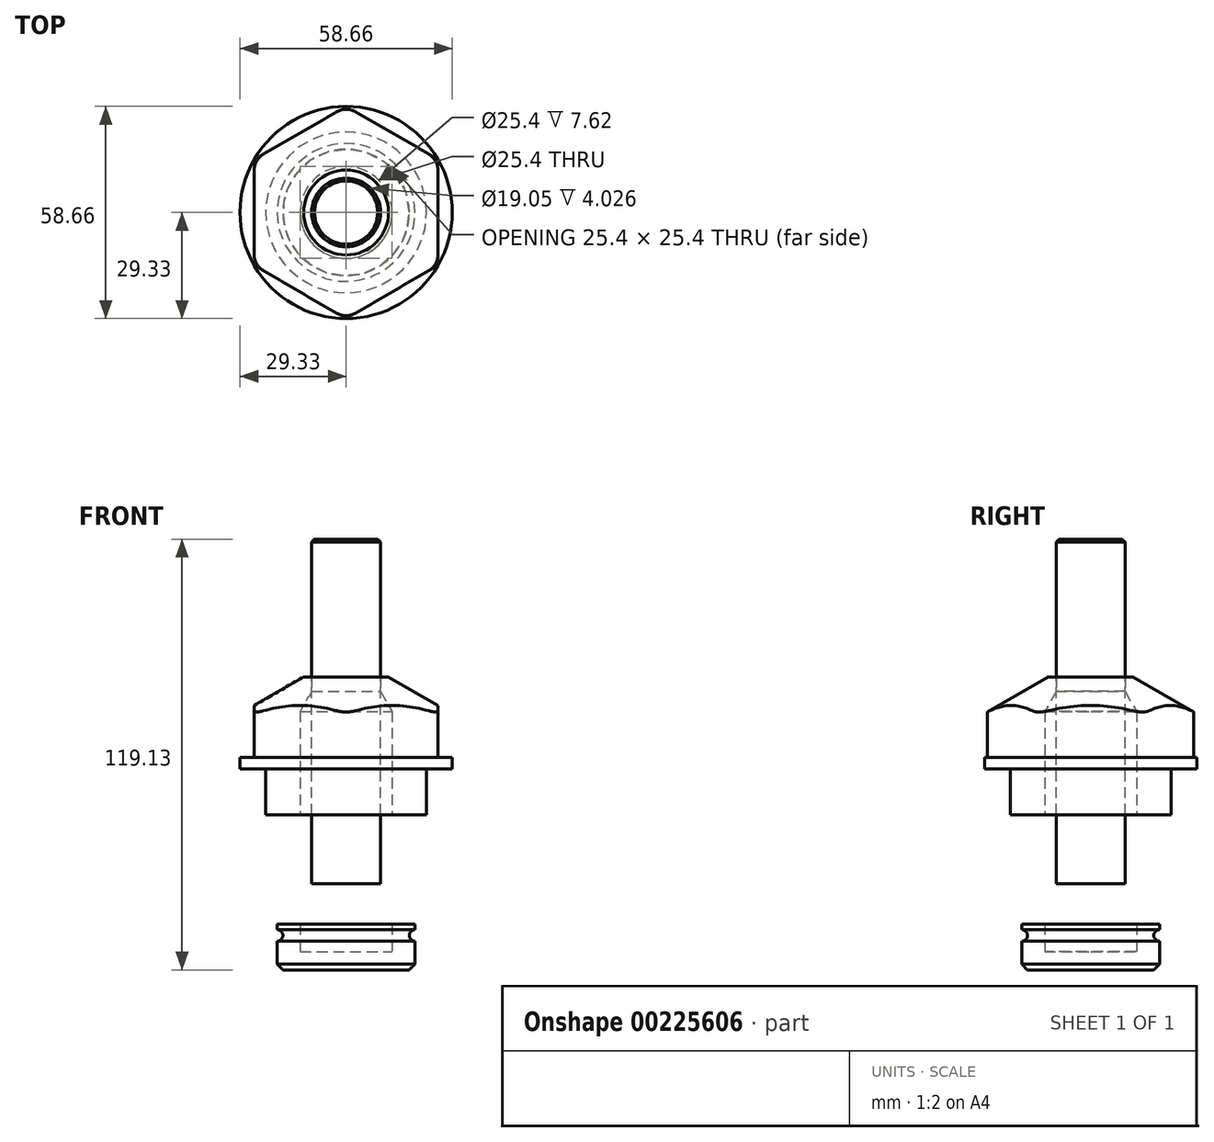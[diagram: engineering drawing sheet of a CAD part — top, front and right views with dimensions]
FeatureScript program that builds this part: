
annotation { "Feature Type Name" : "Feature", "Feature Type Description" : "" }
export const myFeature = defineFeature(function(context is Context, id is Id, definition is map)
    precondition{}
    {
        {
            var Q0;
            Q0=qCreatedBy(makeId("Top.planeOp"),FACE);
            var sketch = newSketch(context, id + "F0", { "sketchPlane" : qUnion([Q0])});
            skCircle(sketch, "E0", {"center": v(0, 0) * mm, "radius": 29.33 * mm});
            skLineSegment(sketch, "E1", {"start": v(0, 29.33) * mm, "end": v(0, -29.33) * mm, "construction": true});
            skLineSegment(sketch, "E2", {"start": v(-25.4, 14.66) * mm, "end": v(25.4, -14.66) * mm, "construction": true});
            skLineSegment(sketch, "E3", {"start": v(-25.4, -14.66) * mm, "end": v(25.4, 14.66) * mm, "construction": true});
            skLineSegment(sketch, "E4", {"start": v(-25.4, 14.66) * mm, "end": v(0, 29.33) * mm});
            skLineSegment(sketch, "E5", {"start": v(0, 29.33) * mm, "end": v(25.4, 14.66) * mm});
            skLineSegment(sketch, "E6", {"start": v(25.4, 14.66) * mm, "end": v(25.4, -14.66) * mm});
            skLineSegment(sketch, "E7", {"start": v(25.4, -14.66) * mm, "end": v(0, -29.33) * mm});
            skLineSegment(sketch, "E8", {"start": v(0, -29.33) * mm, "end": v(-25.4, -14.66) * mm});
            skLineSegment(sketch, "E9", {"start": v(-25.4, -14.66) * mm, "end": v(-25.4, 14.66) * mm});
            skCircle(sketch, "E10", {"center": v(0, 0) * mm, "radius": 7.94 * mm});
            skSolve(sketch);
        }
        {
            var Q0;
            Q0=makeQuery(id+"F0.imprint","IMPRINT",FACE,{"disambiguationData":[TD([[makeQuery(id+"F0.imprint","IMPRINT",EDGE,{"derivedFrom":sQuery(id+"F0.wireOp",EDGE,"E10")}),1.0]])]});
            var Q1;
            Q1=makeQuery(id+"F0.imprint","IMPRINT",FACE,{"disambiguationData":[TD([[makeQuery(id+"F0.imprint","IMPRINT",EDGE,{"derivedFrom":sQuery(id+"F0.wireOp",EDGE,"E4")}),-1.0]])]});
            extrude(context, id + "F1", {"entities" : qUnion([Q0, Q1]), "flatOperationType" : FlatOperationType.REMOVE, "depth" : 25.4 * mm, "offsetDistance" : 25.4 * mm, "domain" : OperationDomain.MODEL});
        }
        {
            var Q0;
            {var subQ0=sQuery(id+"F0.wireOp",EDGE,"E8");Q0=makeQuery(id+"F0.imprint","IMPRINT",FACE,{"disambiguationData":[TD([[makeQuery(id+"F0.imprint","IMPRINT",EDGE,{"derivedFrom":subQ0}),1.0]])]});}
            var Q1;
            {var subQ0=sQuery(id+"F0.wireOp",EDGE,"E7");Q1=makeQuery(id+"F0.imprint","IMPRINT",FACE,{"disambiguationData":[TD([[makeQuery(id+"F0.imprint","IMPRINT",EDGE,{"derivedFrom":subQ0}),1.0]])]});}
            var Q2;
            {var subQ0=sQuery(id+"F0.wireOp",EDGE,"E6");Q2=makeQuery(id+"F0.imprint","IMPRINT",FACE,{"disambiguationData":[TD([[makeQuery(id+"F0.imprint","IMPRINT",EDGE,{"derivedFrom":subQ0}),1.0]])]});}
            var Q3;
            Q3=makeQuery(id+"F0.imprint","IMPRINT",FACE,{"disambiguationData":[TD([[makeQuery(id+"F0.imprint","IMPRINT",EDGE,{"derivedFrom":sQuery(id+"F0.wireOp",EDGE,"E4")}),-1.0]])]});
            var Q4;
            {var subQ0=sQuery(id+"F0.wireOp",EDGE,"E5");Q4=makeQuery(id+"F0.imprint","IMPRINT",FACE,{"disambiguationData":[TD([[makeQuery(id+"F0.imprint","IMPRINT",EDGE,{"derivedFrom":subQ0}),1.0]])]});}
            var Q5;
            {var subQ0=sQuery(id+"F0.wireOp",EDGE,"E4");Q5=makeQuery(id+"F0.imprint","IMPRINT",FACE,{"disambiguationData":[TD([[makeQuery(id+"F0.imprint","IMPRINT",EDGE,{"derivedFrom":subQ0}),1.0]])]});}
            var Q6;
            {var subQ0=sQuery(id+"F0.wireOp",EDGE,"E9");Q6=makeQuery(id+"F0.imprint","IMPRINT",FACE,{"disambiguationData":[TD([[makeQuery(id+"F0.imprint","IMPRINT",EDGE,{"derivedFrom":subQ0}),1.0]])]});}
            extrude(context, id + "F2", {"entities" : qUnion([Q0, Q1, Q2, Q3, Q4, Q5, Q6]), "operationType" : NewBodyOperationType.ADD, "flatOperationType" : FlatOperationType.REMOVE, "depth" : 3.17 * mm, "offsetDistance" : 25.4 * mm, "domain" : OperationDomain.MODEL});
        }
        {
            var Q0;
            Q0=makeQuery(id+"F1.opExtrude","SWEPT_EDGE",EDGE,{"disambiguationData":[OSD([sQuery(id+"F0.wireOp",EDGE,"E0"),sQuery(id+"F0.wireOp",EDGE,"E7"),sQuery(id+"F0.wireOp",EDGE,"E8")])]});
            var Q1;
            Q1=makeQuery(id+"F1.opExtrude","SWEPT_EDGE",EDGE,{"disambiguationData":[OSD([sQuery(id+"F0.wireOp",EDGE,"E0"),sQuery(id+"F0.wireOp",EDGE,"E6"),sQuery(id+"F0.wireOp",EDGE,"E7")])]});
            var Q2;
            Q2=makeQuery(id+"F1.opExtrude","SWEPT_EDGE",EDGE,{"disambiguationData":[OSD([sQuery(id+"F0.wireOp",EDGE,"E0"),sQuery(id+"F0.wireOp",EDGE,"E5"),sQuery(id+"F0.wireOp",EDGE,"E6")])]});
            var Q3;
            Q3=makeQuery(id+"F1.opExtrude","SWEPT_EDGE",EDGE,{"disambiguationData":[OSD([sQuery(id+"F0.wireOp",EDGE,"E0"),sQuery(id+"F0.wireOp",EDGE,"E4"),sQuery(id+"F0.wireOp",EDGE,"E5")])]});
            var Q4;
            Q4=makeQuery(id+"F1.opExtrude","SWEPT_EDGE",EDGE,{"disambiguationData":[OSD([sQuery(id+"F0.wireOp",EDGE,"E0"),sQuery(id+"F0.wireOp",EDGE,"E4"),sQuery(id+"F0.wireOp",EDGE,"E9")])]});
            var Q5;
            Q5=makeQuery(id+"F1.opExtrude","SWEPT_EDGE",EDGE,{"disambiguationData":[OSD([sQuery(id+"F0.wireOp",EDGE,"E0"),sQuery(id+"F0.wireOp",EDGE,"E8"),sQuery(id+"F0.wireOp",EDGE,"E9")])]});
            fillet(context, id + "F3", {"entities" : qUnion([Q0, Q1, Q2, Q3, Q4, Q5]), "radius" : 5.08 * mm, "tangentPropagation" : true, "defaultsChanged" : false, "vertexSettings" : [], "allowEdgeOverflow" : false});
        }
        {
            var Q0;
            Q0=qCreatedBy(makeId("Right.planeOp"),FACE);
            var sketch = newSketch(context, id + "F4", { "sketchPlane" : qUnion([Q0])});
            skLineSegment(sketch, "E11", {"start": v(0, 52) * mm, "end": v(0, 0) * mm, "construction": true});
            skLineSegment(sketch, "E12", {"start": v(11.73, 25.4) * mm, "end": v(35.4, 11.74) * mm});
            skLineSegment(sketch, "E13", {"start": v(35.4, 11.74) * mm, "end": v(35.4, 25.4) * mm});
            skLineSegment(sketch, "E14", {"start": v(35.4, 25.4) * mm, "end": v(11.73, 25.4) * mm});
            skLineSegment(sketch, "E15.0", {"start": v(11.73, 25.4) * mm, "end": v(-11.73, 25.4) * mm});
            skLineSegment(sketch, "E16.bottom", {"start": v(0, 0) * mm, "end": v(22.23, 0) * mm});
            skLineSegment(sketch, "E16.top", {"start": v(0, -12.7) * mm, "end": v(22.23, -12.7) * mm});
            skLineSegment(sketch, "E16.left", {"start": v(0, 0) * mm, "end": v(0, -12.7) * mm});
            skLineSegment(sketch, "E16.right", {"start": v(22.23, 0) * mm, "end": v(22.23, -12.7) * mm});
            skLineSegment(sketch, "E17.bottom", {"start": v(0, -12.7) * mm, "end": v(19.05, -12.7) * mm});
            skLineSegment(sketch, "E17.top", {"start": v(0, -27.69) * mm, "end": v(19.05, -27.69) * mm});
            skLineSegment(sketch, "E17.left", {"start": v(0, -12.7) * mm, "end": v(0, -27.69) * mm});
            skLineSegment(sketch, "E17.right", {"start": v(19.05, -12.7) * mm, "end": v(19.05, -27.69) * mm});
            skLineSegment(sketch, "E18.bottom", {"start": v(17.78, -27.69) * mm, "end": v(0, -27.69) * mm});
            skLineSegment(sketch, "E18.top", {"start": v(17.78, -42.93) * mm, "end": v(0, -42.93) * mm});
            skLineSegment(sketch, "E18.left", {"start": v(17.78, -27.69) * mm, "end": v(17.78, -42.93) * mm});
            skLineSegment(sketch, "E18.right", {"start": v(0, -27.69) * mm, "end": v(0, -42.93) * mm});
            skLineSegment(sketch, "E19.bottom", {"start": v(0, -42.93) * mm, "end": v(19.05, -42.93) * mm});
            skLineSegment(sketch, "E19.top", {"start": v(0, -55.63) * mm, "end": v(19.05, -55.63) * mm});
            skLineSegment(sketch, "E19.left", {"start": v(0, -42.93) * mm, "end": v(0, -55.63) * mm});
            skLineSegment(sketch, "E19.right", {"start": v(19.05, -42.93) * mm, "end": v(19.05, -55.63) * mm});
            skCircle(sketch, "E20", {"center": v(19.05, -24.51) * mm, "radius": 1.59 * mm});
            skCircle(sketch, "E21", {"center": v(19.05, -46.1) * mm, "radius": 1.59 * mm});
            skCircle(sketch, "E22", {"center": v(0, -17.46) * mm, "radius": 3.18 * mm});
            skCircle(sketch, "E23", {"center": v(0, -35.3) * mm, "radius": 3.18 * mm});
            skSolve(sketch);
        }
        {
            var Q0;
            Q0=makeQuery(id+"F4.imprint","IMPRINT",FACE,{"disambiguationData":[TD([[makeQuery(id+"F4.imprint","IMPRINT",EDGE,{"derivedFrom":sQuery(id+"F4.wireOp",EDGE,"E12")}),1.0]])]});
            var Q1;
            Q1=sQuery(id+"F4.wireOp",EDGE,"E11");
            revolve(context, id + "F5", {"operationType" : NewBodyOperationType.REMOVE, "surfaceOperationType" : NewSurfaceOperationType.NEW, "entities" : qUnion([Q0]), "axis" : qUnion([Q1]), "revolveType" : RevolveType.FULL, "oppositeDirection" : true});
        }
        {
            var Q0;
            {var subQ7=sQuery(id+"F4.wireOp",EDGE,"E18.bottom");Q0=makeQuery(id+"F4.imprint","IMPRINT",FACE,{"disambiguationData":[TD([[makeQuery(id+"F4.imprint","IMPRINT",EDGE,{"derivedFrom":subQ7}),1.0]])]});}
            var Q1;
            {var subQ10=sQuery(id+"F4.wireOp",EDGE,"E17.bottom");Q1=makeQuery(id+"F4.imprint","IMPRINT",FACE,{"disambiguationData":[TD([[makeQuery(id+"F4.imprint","IMPRINT",EDGE,{"derivedFrom":subQ10}),-1.0]])]});}
            var Q2;
            Q2=makeQuery(id+"F4.imprint","IMPRINT",FACE,{"disambiguationData":[TD([[makeQuery(id+"F4.imprint","IMPRINT",EDGE,{"derivedFrom":sQuery(id+"F4.wireOp",EDGE,"E16.bottom")}),-1.0]])]});
            var Q3;
            {var subQ4=sQuery(id+"F4.wireOp",EDGE,"E19.top");Q3=makeQuery(id+"F4.imprint","IMPRINT",FACE,{"disambiguationData":[TD([[makeQuery(id+"F4.imprint","IMPRINT",EDGE,{"derivedFrom":subQ4}),1.0]])]});}
            var Q4;
            Q4=sQuery(id+"F4.wireOp",EDGE,"E11");
            revolve(context, id + "F6", {"operationType" : NewBodyOperationType.ADD, "surfaceOperationType" : NewSurfaceOperationType.NEW, "entities" : qUnion([Q0, Q1, Q2, Q3]), "axis" : qUnion([Q4]), "revolveType" : RevolveType.FULL});
        }
        {
            var Q0;
            Q0=makeQuery(id+"F6.opRevolve","SWEPT_EDGE",EDGE,{"disambiguationData":[OSD([sQuery(id+"F4.wireOp",EDGE,"E19.top"),sQuery(id+"F4.wireOp",EDGE,"E19.right")])]});
            chamfer(context, id + "F7", {"entities" : qUnion([Q0]), "width" : 1.59 * mm, "tangentPropagation" : true});
        }
        {
            var Q0;
            {var subQ0=sQuery(id+"F4.wireOp",EDGE,"E16.right");var subQ1=sQuery(id+"F4.wireOp",EDGE,"E20");var subQ3=makeQuery(id+"F4.imprint","INTERSECT",VERTEX,{"disambiguationData":[OD(0.0)],"derivedFrom":[subQ0,subQ1]});Q0=makeQuery(id+"F4.imprint","IMPRINT",FACE,{"disambiguationData":[TD([[makeQuery(id+"F4.imprint","SKETCH_ENTITY",EDGE,{"disambiguationData":[TD([[subQ3,-1.0]])],"sketchEntityId":"E16.right"}),1.0]])]});}
            var Q1;
            {var subQ0=sQuery(id+"F4.wireOp",EDGE,"E20");var subQ1=sQuery(id+"F4.wireOp",EDGE,"E17.right");var subQ3=makeQuery(id+"F4.imprint","INTERSECT",VERTEX,{"disambiguationData":[OD(0.0)],"derivedFrom":[subQ1,subQ0]});Q1=makeQuery(id+"F4.imprint","IMPRINT",FACE,{"disambiguationData":[TD([[makeQuery(id+"F4.imprint","IMPRINT",EDGE,{"disambiguationData":[TD([[subQ3,-1.0]])],"derivedFrom":subQ1}),-1.0]])]});}
            var Q2;
            {var subQ0=sQuery(id+"F4.wireOp",EDGE,"E20");var subQ1=sQuery(id+"F4.wireOp",EDGE,"E17.right");var subQ3=makeQuery(id+"F4.imprint","INTERSECT",VERTEX,{"disambiguationData":[OD(0.0)],"derivedFrom":[subQ1,subQ0]});Q2=makeQuery(id+"F4.imprint","IMPRINT",FACE,{"disambiguationData":[TD([[makeQuery(id+"F4.imprint","IMPRINT",EDGE,{"disambiguationData":[TD([[subQ3,-1.0]])],"derivedFrom":subQ1}),1.0]])]});}
            var Q3;
            Q3=sQuery(id+"F4.wireOp",EDGE,"E11");
            revolve(context, id + "F8", {"surfaceOperationType" : NewSurfaceOperationType.NEW, "entities" : qUnion([Q0, Q1, Q2]), "axis" : qUnion([Q3]), "revolveType" : RevolveType.FULL});
        }
        {
            var Q0;
            {var subQ0=sQuery(id+"F4.wireOp",EDGE,"E22");var subQ1=sQuery(id+"F4.wireOp",EDGE,"E17.left");var subQ3=makeQuery(id+"F4.imprint","INTERSECT",VERTEX,{"disambiguationData":[OD(0.0)],"derivedFrom":[subQ1,subQ0]});Q0=makeQuery(id+"F4.imprint","IMPRINT",FACE,{"disambiguationData":[TD([[makeQuery(id+"F4.imprint","IMPRINT",EDGE,{"disambiguationData":[TD([[subQ3,-1.0]])],"derivedFrom":subQ1}),-1.0]])]});}
            var Q1;
            {var subQ0=sQuery(id+"F4.wireOp",EDGE,"E22");var subQ1=sQuery(id+"F4.wireOp",EDGE,"E17.left");var subQ3=makeQuery(id+"F4.imprint","INTERSECT",VERTEX,{"disambiguationData":[OD(0.0)],"derivedFrom":[subQ1,subQ0]});Q1=makeQuery(id+"F4.imprint","IMPRINT",FACE,{"disambiguationData":[TD([[makeQuery(id+"F4.imprint","IMPRINT",EDGE,{"disambiguationData":[TD([[subQ3,-1.0]])],"derivedFrom":subQ1}),1.0]])]});}
            var Q2;
            {var subQ0=sQuery(id+"F4.wireOp",EDGE,"E23");var subQ1=sQuery(id+"F4.wireOp",EDGE,"E18.right");var subQ3=makeQuery(id+"F4.imprint","INTERSECT",VERTEX,{"disambiguationData":[OD(0.0)],"derivedFrom":[subQ1,subQ0]});Q2=makeQuery(id+"F4.imprint","IMPRINT",FACE,{"disambiguationData":[TD([[makeQuery(id+"F4.imprint","IMPRINT",EDGE,{"disambiguationData":[TD([[subQ3,-1.0]])],"derivedFrom":subQ1}),-1.0]])]});}
            var Q3;
            {var subQ0=sQuery(id+"F4.wireOp",EDGE,"E23");var subQ1=sQuery(id+"F4.wireOp",EDGE,"E18.right");var subQ3=makeQuery(id+"F4.imprint","INTERSECT",VERTEX,{"disambiguationData":[OD(0.0)],"derivedFrom":[subQ1,subQ0]});Q3=makeQuery(id+"F4.imprint","IMPRINT",FACE,{"disambiguationData":[TD([[makeQuery(id+"F4.imprint","IMPRINT",EDGE,{"disambiguationData":[TD([[subQ3,-1.0]])],"derivedFrom":subQ1}),1.0]])]});}
            extrude(context, id + "F9", {"entities" : qUnion([Q0, Q1, Q2, Q3]), "operationType" : NewBodyOperationType.REMOVE, "flatOperationType" : FlatOperationType.REMOVE, "endBound" : BoundingType.THROUGH_ALL, "depth" : 25.4 * mm, "offsetDistance" : 25.4 * mm, "domain" : OperationDomain.MODEL});
        }
        {
            var Q0;
            Q0=qCreatedBy(makeId("Right.planeOp"),FACE);
            var sketch = newSketch(context, id + "F10", { "sketchPlane" : qUnion([Q0])});
            skLineSegment(sketch, "E24", {"start": v(0, 63.5) * mm, "end": v(0, -50.55) * mm});
            skLineSegment(sketch, "E25", {"start": v(0, -50.55) * mm, "end": v(12.7, -50.55) * mm});
            skLineSegment(sketch, "E26", {"start": v(12.7, -50.55) * mm, "end": v(12.7, 15.88) * mm});
            skLineSegment(sketch, "E27", {"start": v(12.7, 15.88) * mm, "end": v(0, 15.88) * mm});
            skLineSegment(sketch, "E28", {"start": v(9.53, -31.75) * mm, "end": v(9.53, 63.5) * mm});
            skLineSegment(sketch, "E29", {"start": v(9.52, 63.5) * mm, "end": v(0, 63.5) * mm});
            skLineSegment(sketch, "E30", {"start": v(9.53, 21.37) * mm, "end": v(12.7, 15.88) * mm});
            skLineSegment(sketch, "E31.rect.bottom", {"start": v(12.7, -38.1) * mm, "end": v(-12.7, -38.1) * mm});
            skLineSegment(sketch, "E31.rect.top", {"start": v(12.7, -31.75) * mm, "end": v(-12.7, -31.75) * mm});
            skLineSegment(sketch, "E31.rect.left", {"start": v(12.7, -38.1) * mm, "end": v(12.7, -31.75) * mm});
            skLineSegment(sketch, "E31.rect.right", {"start": v(-12.7, -38.1) * mm, "end": v(-12.7, -31.75) * mm});
            skPoint(sketch, "E31.rect.middle", {"position": v(0, -34.92) * mm});
            skSolve(sketch);
        }
        {
            var Q0;
            {var subQ0=sQuery(id+"F10.wireOp",EDGE,"E29");Q0=makeQuery(id+"F10.imprint","IMPRINT",FACE,{"disambiguationData":[TD([[makeQuery(id+"F10.imprint","IMPRINT",EDGE,{"derivedFrom":subQ0}),1.0]])]});}
            var Q1;
            {var subQ0=sQuery(id+"F10.wireOp",EDGE,"E30");Q1=makeQuery(id+"F10.imprint","IMPRINT",FACE,{"disambiguationData":[TD([[makeQuery(id+"F10.imprint","IMPRINT",EDGE,{"derivedFrom":subQ0}),-1.0]])]});}
            var Q2;
            {var subQ1=sQuery(id+"F10.wireOp",EDGE,"E24");var subQ5=sQuery(id+"F10.wireOp",EDGE,"E27");var subQ7=makeQuery(id+"F10.imprint","INTERSECT",VERTEX,{"derivedFrom":[subQ1,subQ5]});Q2=makeQuery(id+"F10.imprint","IMPRINT",FACE,{"disambiguationData":[TD([[makeQuery(id+"F10.imprint","IMPRINT",EDGE,{"disambiguationData":[TD([[subQ7,-1.0]])],"derivedFrom":subQ1}),1.0]])]});}
            var Q3;
            {var subQ0=sQuery(id+"F10.wireOp",EDGE,"E31.rect.top");var subQ3=sQuery(id+"F10.wireOp",EDGE,"E28");var subQ4=makeQuery(id+"F10.imprint","INTERSECT",VERTEX,{"derivedFrom":[subQ3,subQ0]});Q3=makeQuery(id+"F10.imprint","IMPRINT",FACE,{"disambiguationData":[TD([[makeQuery(id+"F10.imprint","IMPRINT",EDGE,{"disambiguationData":[TD([[subQ4,-1.0]])],"derivedFrom":subQ3}),-1.0]])]});}
            var Q4;
            {var subQ5=sQuery(id+"F10.wireOp",EDGE,"E25");Q4=makeQuery(id+"F10.imprint","IMPRINT",FACE,{"disambiguationData":[TD([[makeQuery(id+"F10.imprint","IMPRINT",EDGE,{"derivedFrom":subQ5}),1.0]])]});}
            var Q5;
            {var subQ0=sQuery(id+"F10.wireOp",EDGE,"E31.rect.left");Q5=makeQuery(id+"F10.imprint","IMPRINT",FACE,{"disambiguationData":[TD([[makeQuery(id+"F10.imprint","IMPRINT",EDGE,{"derivedFrom":subQ0}),1.0]])]});}
            var Q6;
            Q6=sQuery(id+"F10.wireOp",EDGE,"E24");
            revolve(context, id + "F11", {"operationType" : NewBodyOperationType.REMOVE, "surfaceOperationType" : NewSurfaceOperationType.NEW, "entities" : qUnion([Q0, Q1, Q2, Q3, Q4, Q5]), "axis" : qUnion([Q6]), "revolveType" : RevolveType.FULL, "oppositeDirection" : true});
        }
        {
            var Q0;
            {var subQ0=sQuery(id+"F10.wireOp",EDGE,"E29");Q0=makeQuery(id+"F10.imprint","IMPRINT",FACE,{"disambiguationData":[TD([[makeQuery(id+"F10.imprint","IMPRINT",EDGE,{"derivedFrom":subQ0}),1.0]])]});}
            var Q1;
            {var subQ1=sQuery(id+"F10.wireOp",EDGE,"E24");var subQ5=sQuery(id+"F10.wireOp",EDGE,"E27");var subQ7=makeQuery(id+"F10.imprint","INTERSECT",VERTEX,{"derivedFrom":[subQ1,subQ5]});Q1=makeQuery(id+"F10.imprint","IMPRINT",FACE,{"disambiguationData":[TD([[makeQuery(id+"F10.imprint","IMPRINT",EDGE,{"disambiguationData":[TD([[subQ7,-1.0]])],"derivedFrom":subQ1}),1.0]])]});}
            var Q2;
            {var subQ0=sQuery(id+"F10.wireOp",EDGE,"E31.rect.left");Q2=makeQuery(id+"F10.imprint","IMPRINT",FACE,{"disambiguationData":[TD([[makeQuery(id+"F10.imprint","IMPRINT",EDGE,{"derivedFrom":subQ0}),1.0]])]});}
            var Q3;
            Q3=sQuery(id+"F10.wireOp",EDGE,"E24");
            revolve(context, id + "F12", {"surfaceOperationType" : NewSurfaceOperationType.NEW, "entities" : qUnion([Q0, Q1, Q2]), "axis" : qUnion([Q3]), "revolveType" : RevolveType.FULL});
        }
        {
            var Q0;
            Q0=makeQuery(id+"F12.opRevolve","SWEPT_FACE",FACE,{"disambiguationData":[OSD([sQuery(id+"F10.wireOp",EDGE,"E29")])]});
            chamfer(context, id + "F13", {"entities" : qUnion([Q0]), "width" : 0.8 * mm, "tangentPropagation" : true});
        }
    });
